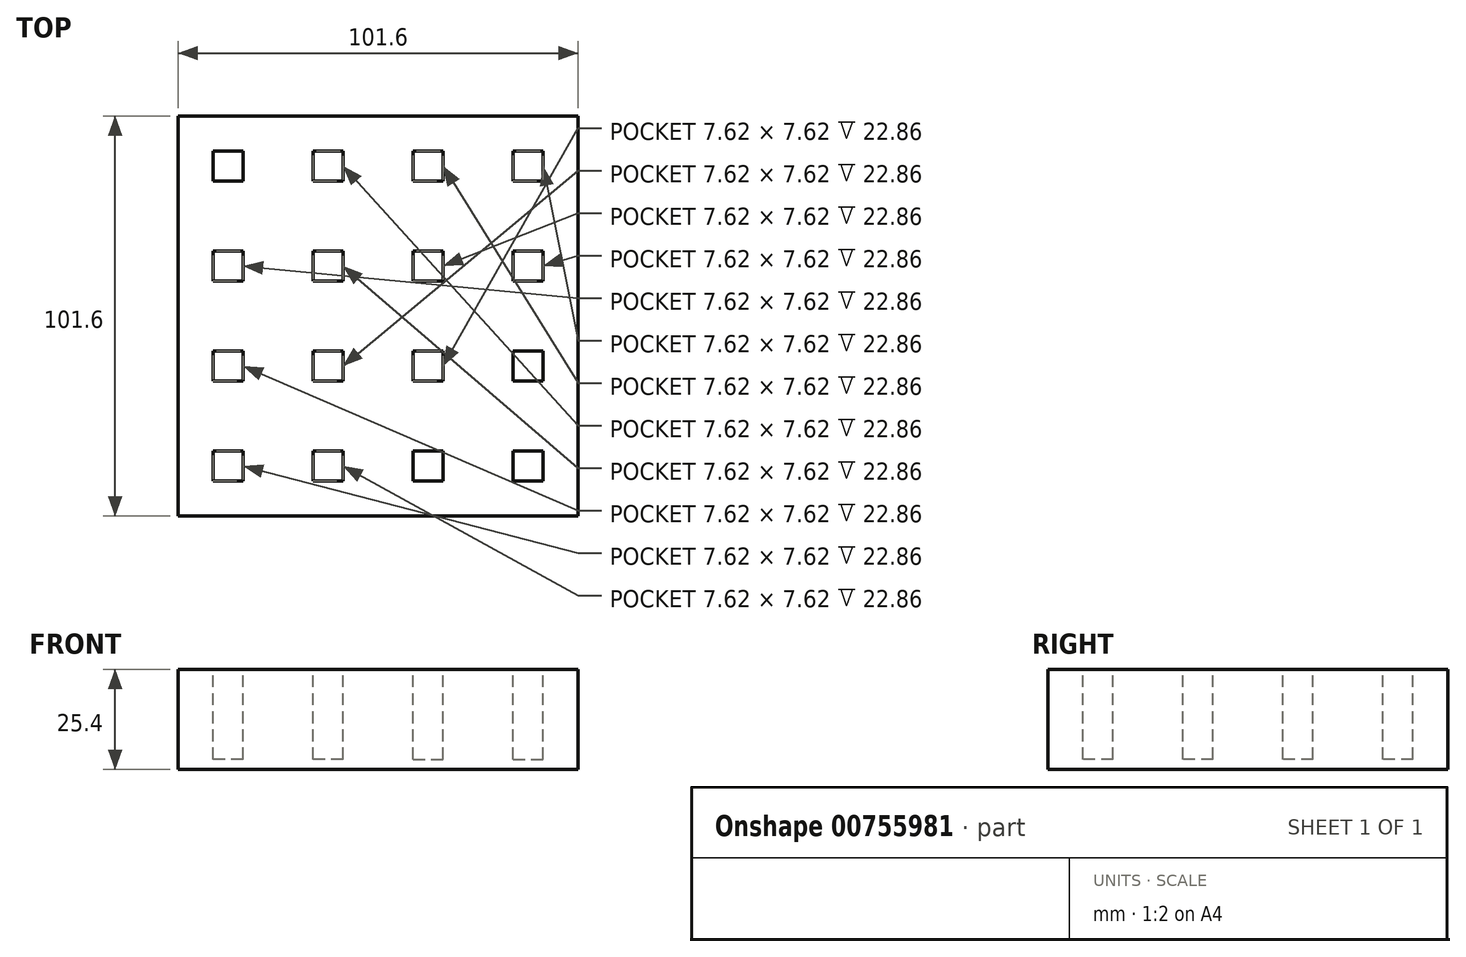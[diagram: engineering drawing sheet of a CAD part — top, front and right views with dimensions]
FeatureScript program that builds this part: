
annotation { "Feature Type Name" : "Feature", "Feature Type Description" : "" }
export const myFeature = defineFeature(function(context is Context, id is Id, definition is map)
    precondition{}
    {
        {
            var Q0;
            Q0=qCreatedBy(makeId("Front.planeOp"),FACE);
            var sketch = newSketch(context, id + "F0", { "sketchPlane" : qUnion([Q0])});
            skLineSegment(sketch, "E0", {"start": v(0, 0) * mm, "end": v(50.8, 0) * mm});
            skLineSegment(sketch, "E1", {"start": v(50.8, 0) * mm, "end": v(50.8, -25.4) * mm});
            skLineSegment(sketch, "E2", {"start": v(50.8, -25.4) * mm, "end": v(-50.8, -25.4) * mm});
            skLineSegment(sketch, "E3", {"start": v(-50.8, -25.4) * mm, "end": v(-50.8, 0) * mm});
            skLineSegment(sketch, "E4", {"start": v(-50.8, 0) * mm, "end": v(0, 0) * mm});
            skSolve(sketch);
        }
        {
            var Q0;
            Q0=makeQuery(id+"F0.imprint","IMPRINT",FACE,{"disambiguationData":[TD([[makeQuery(id+"F0.imprint","IMPRINT",EDGE,{"derivedFrom":sQuery(id+"F0.wireOp",EDGE,"E0")}),-1.0]])]});
            extrude(context, id + "F1", {"entities" : qUnion([Q0]), "depth" : 101.6 * mm, "offsetDistance" : 25.4 * mm});
        }
        {
            var Q0;
            Q0=makeQuery(id+"F1.opExtrude","SWEPT_FACE",FACE,{"disambiguationData":[OSD([sQuery(id+"F0.wireOp",EDGE,"E0"),sQuery(id+"F0.wireOp",EDGE,"E4")])]});
            var sketch = newSketch(context, id + "F2", { "sketchPlane" : qUnion([Q0])});
            skLineSegment(sketch, "E5", {"start": v(-50.8, 0) * mm, "end": v(-38.1, 0) * mm});
            skLineSegment(sketch, "E6.bottom", {"start": v(-34.3, -8.9) * mm, "end": v(-41.91, -8.9) * mm});
            skLineSegment(sketch, "E6.top", {"start": v(-34.3, -16.51) * mm, "end": v(-41.91, -16.51) * mm});
            skLineSegment(sketch, "E6.left", {"start": v(-34.3, -8.9) * mm, "end": v(-34.3, -16.51) * mm});
            skLineSegment(sketch, "E6.right", {"start": v(-41.91, -8.9) * mm, "end": v(-41.91, -16.51) * mm});
            skPoint(sketch, "E6.middle", {"position": v(-38.1, -12.7) * mm});
            skLineSegment(sketch, "E7.bottom", {"start": v(-16.51, -8.9) * mm, "end": v(-8.9, -8.9) * mm});
            skLineSegment(sketch, "E7.top", {"start": v(-16.51, -16.5) * mm, "end": v(-8.9, -16.5) * mm});
            skLineSegment(sketch, "E7.left", {"start": v(-16.51, -8.9) * mm, "end": v(-16.51, -16.51) * mm});
            skLineSegment(sketch, "E7.right", {"start": v(-8.9, -8.9) * mm, "end": v(-8.9, -16.51) * mm});
            skPoint(sketch, "E7.middle", {"position": v(-12.7, -12.7) * mm});
            skLineSegment(sketch, "E8.bottom", {"start": v(8.89, -8.9) * mm, "end": v(16.5, -8.9) * mm});
            skLineSegment(sketch, "E8.top", {"start": v(8.89, -16.51) * mm, "end": v(16.5, -16.51) * mm});
            skLineSegment(sketch, "E8.left", {"start": v(8.89, -8.9) * mm, "end": v(8.89, -16.51) * mm});
            skLineSegment(sketch, "E8.right", {"start": v(16.5, -8.9) * mm, "end": v(16.5, -16.51) * mm});
            skPoint(sketch, "E8.middle", {"position": v(12.7, -12.7) * mm});
            skLineSegment(sketch, "E9.bottom", {"start": v(34.29, -8.89) * mm, "end": v(41.9, -8.89) * mm});
            skLineSegment(sketch, "E9.top", {"start": v(34.29, -16.5) * mm, "end": v(41.9, -16.5) * mm});
            skLineSegment(sketch, "E9.left", {"start": v(34.29, -8.89) * mm, "end": v(34.29, -16.5) * mm});
            skLineSegment(sketch, "E9.right", {"start": v(41.9, -8.89) * mm, "end": v(41.9, -16.5) * mm});
            skPoint(sketch, "E9.middle", {"position": v(38.1, -12.7) * mm});
            skLineSegment(sketch, "E10.bottom", {"start": v(-34.3, -34.3) * mm, "end": v(-41.91, -34.3) * mm});
            skLineSegment(sketch, "E10.top", {"start": v(-34.3, -41.91) * mm, "end": v(-41.91, -41.91) * mm});
            skLineSegment(sketch, "E10.left", {"start": v(-34.3, -34.3) * mm, "end": v(-34.3, -41.91) * mm});
            skLineSegment(sketch, "E10.right", {"start": v(-41.91, -34.3) * mm, "end": v(-41.91, -41.91) * mm});
            skPoint(sketch, "E10.middle", {"position": v(-38.1, -38.1) * mm});
            skLineSegment(sketch, "E11.bottom", {"start": v(-16.51, -34.3) * mm, "end": v(-8.9, -34.3) * mm});
            skLineSegment(sketch, "E11.top", {"start": v(-16.51, -41.91) * mm, "end": v(-8.9, -41.91) * mm});
            skLineSegment(sketch, "E11.left", {"start": v(-16.51, -34.3) * mm, "end": v(-16.51, -41.91) * mm});
            skLineSegment(sketch, "E11.right", {"start": v(-8.9, -34.3) * mm, "end": v(-8.9, -41.91) * mm});
            skPoint(sketch, "E11.middle", {"position": v(-12.7, -38.1) * mm});
            skLineSegment(sketch, "E12.bottom", {"start": v(-34.3, -59.69) * mm, "end": v(-41.91, -59.69) * mm});
            skLineSegment(sketch, "E12.top", {"start": v(-34.3, -67.3) * mm, "end": v(-41.91, -67.3) * mm});
            skLineSegment(sketch, "E12.left", {"start": v(-34.3, -59.69) * mm, "end": v(-34.3, -67.3) * mm});
            skLineSegment(sketch, "E12.right", {"start": v(-41.91, -59.69) * mm, "end": v(-41.91, -67.3) * mm});
            skPoint(sketch, "E12.middle", {"position": v(-38.1, -63.5) * mm});
            skLineSegment(sketch, "E13.bottom", {"start": v(-34.3, -85.1) * mm, "end": v(-41.91, -85.1) * mm});
            skLineSegment(sketch, "E13.top", {"start": v(-34.3, -92.71) * mm, "end": v(-41.91, -92.71) * mm});
            skLineSegment(sketch, "E13.left", {"start": v(-34.3, -85.1) * mm, "end": v(-34.3, -92.71) * mm});
            skLineSegment(sketch, "E13.right", {"start": v(-41.91, -85.1) * mm, "end": v(-41.91, -92.71) * mm});
            skPoint(sketch, "E13.middle", {"position": v(-38.1, -88.9) * mm});
            skLineSegment(sketch, "E14.bottom", {"start": v(-16.51, -85.1) * mm, "end": v(-8.9, -85.1) * mm});
            skLineSegment(sketch, "E14.top", {"start": v(-16.51, -92.71) * mm, "end": v(-8.9, -92.71) * mm});
            skLineSegment(sketch, "E14.left", {"start": v(-16.51, -85.1) * mm, "end": v(-16.51, -92.71) * mm});
            skLineSegment(sketch, "E14.right", {"start": v(-8.9, -85.1) * mm, "end": v(-8.9, -92.71) * mm});
            skPoint(sketch, "E14.middle", {"position": v(-12.7, -88.9) * mm});
            skLineSegment(sketch, "E15.bottom", {"start": v(8.89, -85.1) * mm, "end": v(16.5, -85.1) * mm});
            skLineSegment(sketch, "E15.top", {"start": v(8.89, -92.7) * mm, "end": v(16.5, -92.7) * mm});
            skLineSegment(sketch, "E15.left", {"start": v(8.89, -85.1) * mm, "end": v(8.89, -92.7) * mm});
            skLineSegment(sketch, "E15.right", {"start": v(16.5, -85.1) * mm, "end": v(16.5, -92.7) * mm});
            skPoint(sketch, "E15.middle", {"position": v(12.7, -88.9) * mm});
            skLineSegment(sketch, "E16.bottom", {"start": v(34.3, -85.1) * mm, "end": v(41.91, -85.1) * mm});
            skLineSegment(sketch, "E16.top", {"start": v(34.3, -92.71) * mm, "end": v(41.91, -92.71) * mm});
            skLineSegment(sketch, "E16.left", {"start": v(34.3, -85.1) * mm, "end": v(34.3, -92.71) * mm});
            skLineSegment(sketch, "E16.right", {"start": v(41.91, -85.1) * mm, "end": v(41.91, -92.71) * mm});
            skPoint(sketch, "E16.middle", {"position": v(38.1, -88.9) * mm});
            skLineSegment(sketch, "E17.bottom", {"start": v(34.3, -59.7) * mm, "end": v(41.91, -59.7) * mm});
            skLineSegment(sketch, "E17.top", {"start": v(34.3, -67.31) * mm, "end": v(41.91, -67.31) * mm});
            skLineSegment(sketch, "E17.left", {"start": v(34.3, -59.7) * mm, "end": v(34.3, -67.31) * mm});
            skLineSegment(sketch, "E17.right", {"start": v(41.91, -59.7) * mm, "end": v(41.91, -67.31) * mm});
            skPoint(sketch, "E17.middle", {"position": v(38.1, -63.5) * mm});
            skLineSegment(sketch, "E18.bottom", {"start": v(16.5, -59.7) * mm, "end": v(8.89, -59.7) * mm});
            skLineSegment(sketch, "E18.top", {"start": v(16.5, -67.31) * mm, "end": v(8.89, -67.31) * mm});
            skLineSegment(sketch, "E18.left", {"start": v(16.5, -59.7) * mm, "end": v(16.5, -67.31) * mm});
            skLineSegment(sketch, "E18.right", {"start": v(8.89, -59.7) * mm, "end": v(8.89, -67.31) * mm});
            skPoint(sketch, "E18.middle", {"position": v(12.7, -63.5) * mm});
            skLineSegment(sketch, "E19.bottom", {"start": v(-8.9, -59.7) * mm, "end": v(-16.51, -59.7) * mm});
            skLineSegment(sketch, "E19.top", {"start": v(-8.9, -67.3) * mm, "end": v(-16.51, -67.3) * mm});
            skLineSegment(sketch, "E19.left", {"start": v(-8.9, -59.7) * mm, "end": v(-8.9, -67.3) * mm});
            skLineSegment(sketch, "E19.right", {"start": v(-16.51, -59.7) * mm, "end": v(-16.51, -67.3) * mm});
            skPoint(sketch, "E19.middle", {"position": v(-12.7, -63.5) * mm});
            skLineSegment(sketch, "E20.bottom", {"start": v(16.5, -34.3) * mm, "end": v(8.89, -34.3) * mm});
            skLineSegment(sketch, "E20.top", {"start": v(16.5, -41.91) * mm, "end": v(8.89, -41.91) * mm});
            skLineSegment(sketch, "E20.left", {"start": v(16.5, -34.3) * mm, "end": v(16.5, -41.91) * mm});
            skLineSegment(sketch, "E20.right", {"start": v(8.89, -34.3) * mm, "end": v(8.89, -41.91) * mm});
            skPoint(sketch, "E20.middle", {"position": v(12.7, -38.1) * mm});
            skLineSegment(sketch, "E21.bottom", {"start": v(34.3, -34.3) * mm, "end": v(41.91, -34.3) * mm});
            skLineSegment(sketch, "E21.top", {"start": v(34.3, -41.91) * mm, "end": v(41.91, -41.91) * mm});
            skLineSegment(sketch, "E21.left", {"start": v(34.3, -34.3) * mm, "end": v(34.3, -41.91) * mm});
            skLineSegment(sketch, "E21.right", {"start": v(41.91, -34.3) * mm, "end": v(41.91, -41.91) * mm});
            skPoint(sketch, "E21.middle", {"position": v(38.1, -38.1) * mm});
            skSolve(sketch);
        }
        {
            var Q0;
            Q0 = qSketchRegion(id + "F2", true);
            extrude(context, id + "F3", {"entities" : qUnion([Q0]), "operationType" : NewBodyOperationType.REMOVE, "oppositeDirection" : true, "depth" : 22.86 * mm, "offsetDistance" : 25.4 * mm});
        }
    });
